# Revit family: 8.Кронштейн для потолочного или стенового крепления вентилятора KRK
name_source: partatom
category: Оборудование
revit_build: Autodesk Revit 2016 (Build: 20161004_0715(x64)
units: mm (PartAtom-declared; Revit-internal decimal feet)

## family parameters
Всегда вертикально = Да
На основе рабочей плоскости = Нет
Общий = Нет
При загрузке вырезать с полостями = Нет
Размер круглого соединителя = Использовать диаметр
Тип детали = Нормальный
Точка расчета площади = Нет

## types (6) — shared parameters
Единица измерения = шт.
Завод изготовитель = KORF
Ключевая пометка = Вентиляция
Материал = Сталь серая
Наименование и тех.хар-ка = Кронштейн для потолочного или стенового крепления вентилятора
Раздел = ОВ
отступ = 20 мм

## per-type parameters (varying)
| type | x | А | Б | Д | Масса единицы | Тип, марка, обозначение | середина |
| 100 | 346 мм | 164 мм | 432 мм | 102 мм | 0.6 кг | KRK 100 | 216 мм |
| 160 | 416 мм | 209 мм | 520 мм | 162 мм | 0.8 кг | KRK 160 | 260 мм |
| 200 | 416 мм | 209 мм | 520 мм | 202 мм | 0.8 кг | KRK 200 | 260 мм |
| 250 | 416 мм | 209 мм | 520 мм | 252 мм | 1.2 кг | KRK 250 | 260 мм |
| 315 | 469 мм | 242 мм | 586 мм | 317 мм | 1.4 кг | KRK 315 | 293 мм |
| 125 | 346 мм | 164 мм | 432 мм | 127 мм | 0,6 кг | KRK 125 | 216 мм |
